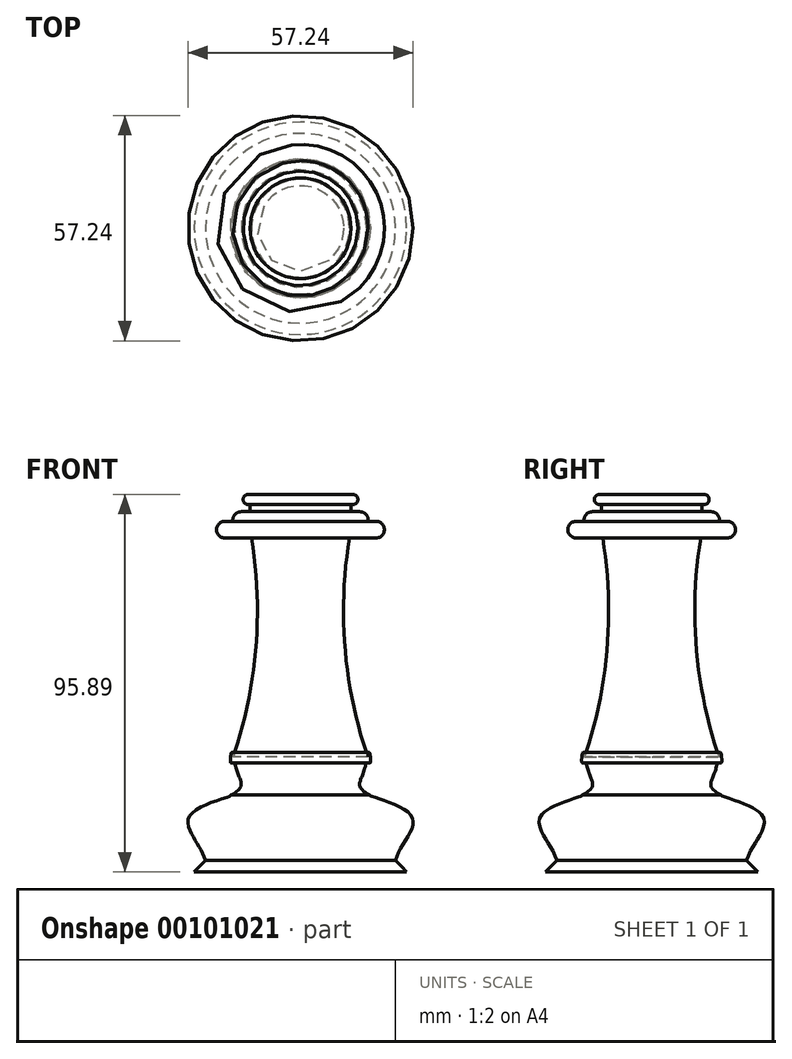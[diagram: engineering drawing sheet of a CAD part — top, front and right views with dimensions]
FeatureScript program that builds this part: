
annotation { "Feature Type Name" : "Feature", "Feature Type Description" : "" }
export const myFeature = defineFeature(function(context is Context, id is Id, definition is map)
    precondition{}
    {
        {
            var Q0;
            Q0=qCreatedBy(makeId("Front.planeOp"),FACE);
            var sketch = newSketch(context, id + "F0", { "sketchPlane" : qUnion([Q0])});
            skLineSegment(sketch, "E0", {"start": v(0, -44.38) * mm, "end": v(-28.1, -44.38) * mm});
            skLineSegment(sketch, "E1", {"start": v(-28.1, -44.38) * mm, "end": v(-28.1, -40.49) * mm});
            skLineSegment(sketch, "E2", {"start": v(-28.1, -40.49) * mm, "end": v(-24.5, -40.49) * mm});
            skFitSpline(sketch, "E3", {"points": [v(-24.5, -40.49) * mm, v(-28.1, -30.05) * mm, v(-17.6, -24.87) * mm, v(-21.95, -24.69) * mm], "startDerivative": vector(-10.67, 29.08) * mm, "endDerivative": vector(-8.79, 1.91) * mm});
            skLineSegment(sketch, "E4", {"start": v(-17.6, -24.87) * mm, "end": v(0, -24.87) * mm});
            skLineSegment(sketch, "E5", {"start": v(0, -24.87) * mm, "end": v(0, -44.38) * mm});
            skFitSpline(sketch, "E6", {"points": [v(-17.6, -24.87) * mm, v(-15.95, -19.28) * mm, v(-17.6, -14.2) * mm, v(-17.6, -16.62) * mm], "startDerivative": vector(29.47, 15.92) * mm, "endDerivative": vector(3.84, 7.09) * mm});
            skLineSegment(sketch, "E7", {"start": v(-17.6, -16.62) * mm, "end": v(0, -16.62) * mm});
            skLineSegment(sketch, "E8", {"start": v(0, -16.62) * mm, "end": v(0, -24.87) * mm});
            skArc(sketch, "E9", {"start": v(-17.6, -16.62) * mm, "mid": v(-11.4, 11.59) * mm, "end": v(-12.44, 40.45) * mm});
            skLineSegment(sketch, "E10", {"start": v(-12.44, 40.45) * mm, "end": v(0, 40.45) * mm});
            skLineSegment(sketch, "E11", {"start": v(-12.44, 40.45) * mm, "end": v(-19.2, 40.45) * mm});
            skLineSegment(sketch, "E12", {"start": v(0, 40.45) * mm, "end": v(0, -16.62) * mm});
            skArc(sketch, "E13", {"start": v(-19.2, 44.7) * mm, "mid": v(-21.32, 42.57) * mm, "end": v(-19.2, 40.45) * mm});
            skLineSegment(sketch, "E14", {"start": v(-19.2, 44.7) * mm, "end": v(0, 44.7) * mm});
            skLineSegment(sketch, "E15", {"start": v(0, 44.7) * mm, "end": v(0, 40.45) * mm});
            skArc(sketch, "E16", {"start": v(-15.11, 47.12) * mm, "mid": v(-16.7, 46.38) * mm, "end": v(-17.17, 44.7) * mm});
            skLineSegment(sketch, "E17", {"start": v(-15.11, 47.12) * mm, "end": v(0, 47.22) * mm});
            skLineSegment(sketch, "E18", {"start": v(0, 47.22) * mm, "end": v(0, 44.7) * mm});
            skLineSegment(sketch, "E19", {"start": v(-12.8, 47.14) * mm, "end": v(-12.81, 49.03) * mm});
            skArc(sketch, "E20", {"start": v(-12.81, 51.42) * mm, "mid": v(-14.57, 50.23) * mm, "end": v(-12.81, 49.03) * mm});
            skLineSegment(sketch, "E21", {"start": v(-12.81, 51.42) * mm, "end": v(0, 51.42) * mm});
            skLineSegment(sketch, "E22", {"start": v(0, 51.42) * mm, "end": v(0, 47.22) * mm});
            skSolve(sketch);
        }
        {
            var Q0;
            Q0 = qSketchRegion(id + "F0", true);
            var Q1;
            Q1=sQuery(id+"F0.wireOp",EDGE,"E5");
            revolve(context, id + "F1", {"entities" : qUnion([Q0]), "axis" : qUnion([Q1]), "revolveType" : RevolveType.FULL});
        }
        {
            var Q0;
            Q0=makeQuery(id+"F1.opRevolve","SWEPT_EDGE",EDGE,{"disambiguationData":[OSD([sQuery(id+"F0.wireOp",EDGE,"E1"),sQuery(id+"F0.wireOp",EDGE,"E2")])]});
            chamfer(context, id + "F2", {"entities" : qUnion([Q0]), "width" : 5 * mm, "tangentPropagation" : true});
        }
    });
